# Revit family: Wood_Lockers-Salsbury_Industries-37000_Series-3_Wide_Units
name_source: partatom
category: Specialty Equipment
revit_build: Autodesk Revit 2016 (Build: 20150714_1515(x64)
units: mm (PartAtom-declared; Revit-internal decimal feet)

## family parameters
Always vertical = Yes
Cut with Voids When Loaded = No
OmniClass Number = 23.40.00.00
OmniClass Title = Equipment and Furnishings
Part Type = Normal
Room Calculation Point = No
Round Connector Dimension = Use Diameter
Shared = No
Work Plane-Based = No

## types (12) — shared parameters
Assembly Code = C1030310
Door Trim = Rubber Trim - Salsbury Finish - Textured
Hardware = Aluminum - Salsbury Finish - Black Satin
Manufacturer = Salsbury Industries
MasterFormat Code = 10 51 23
MasterFormat Title = Lockers
OmniClass 23 Number = 23.40.00.00
OmniClass 23 Title = Equipment and Furnishings
Primary Structure Materials = Particle Board Industrial Grade - Salsbury Finish - White Melamine Inlay
Secondary Structure Materials = Particle Board Industrial Grade - Salsbury Finish - Black Melamine Overlay
Type Comments = Designer Wood Lockers - Double Tier 'S' Style
URL = www.lockers.com
Unit Trim = Melamine - Salsbury Finish - Black
Version = 2.0 (07/14/17)
Width = 36.000"

## per-type parameters (varying)
| type | Base | Base Height | Depth | Description | Door Location D1 | Door Location D2 | Individual Door Height | Model | Sloping Hood Height | Unit Height |
| 37365 | Wood Locker Bases : Base - 36" W x 15" D Lockers | 4.000" | 15.000" | 3 Wide - 6 Feet High - 15 inches Deep - with Base | Wood Locker S-Style Top Doors : Double Tier Top S-Door for Six Foot High Locker | Wood Locker S-Style Bottom Doors : Double Tier Bottom S-Door for Six Foot High Locker | 42.062" | 37365 | 5.743" | 72.000" |
| 37365 - without Base | Wood Locker Bases : None | 0.000" | 15.000" | 3 Wide - 6 Feet High - 15 inches Deep - without Base | Wood Locker S-Style Top Doors : Double Tier Top S-Door for Six Foot High Locker | Wood Locker S-Style Bottom Doors : Double Tier Bottom S-Door for Six Foot High Locker | 42.062" | 37365 without Base | 5.743" | 72.000" |
| 37368 | Wood Locker Bases : Base - 36" W x 18" D Lockers | 4.000" | 18.000" | 3 Wide - 6 Feet High - 18 inches Deep - with Base | Wood Locker S-Style Top Doors : Double Tier Top S-Door for Six Foot High Locker | Wood Locker S-Style Bottom Doors : Double Tier Bottom S-Door for Six Foot High Locker | 42.062" | 37368 | 6.868" | 72.000" |
| 37368 - without Base | Wood Locker Bases : None | 0.000" | 18.000" | 3 Wide - 6 Feet High - 18 inches Deep - without Base | Wood Locker S-Style Top Doors : Double Tier Top S-Door for Six Foot High Locker | Wood Locker S-Style Bottom Doors : Double Tier Bottom S-Door for Six Foot High Locker | 42.062" | 37368 without Base | 6.868" | 72.000" |
| 37361 | Wood Locker Bases : Base - 36" W x 21" D Lockers | 4.000" | 21.000" | 3 Wide - 6 Feet High - 21 inches Deep - with Base | Wood Locker S-Style Top Doors : Double Tier Top S-Door for Six Foot High Locker | Wood Locker S-Style Bottom Doors : Double Tier Bottom S-Door for Six Foot High Locker | 42.062" | 37361 | 7.993" | 72.000" |
| 37361 - without Base | Wood Locker Bases : None | 0.000" | 21.000" | 3 Wide - 6 Feet High - 21 inches Deep - without Base | Wood Locker S-Style Top Doors : Double Tier Top S-Door for Six Foot High Locker | Wood Locker S-Style Bottom Doors : Double Tier Bottom S-Door for Six Foot High Locker | 42.062" | 37361 without Base | 7.993" | 72.000" |
| 37355 | Wood Locker Bases : Base - 36" W x 15" D Lockers | 4.000" | 15.000" | 3 Wide - 5 Feet High - 15 inches Deep - with Base | Wood Locker S-Style Top Doors : Double Tier Top S-Door for Five Foot High Locker | Wood Locker S-Style Bottom Doors : Double Tier Bottom S-Door for Five Foot High Locker | 36.062" | 37355 | 5.743" | 60.000" |
| 37355 - without Base | Wood Locker Bases : None | 0.000" | 15.000" | 3 Wide - 5 Feet High - 15 inches Deep - without Base | Wood Locker S-Style Top Doors : Double Tier Top S-Door for Five Foot High Locker | Wood Locker S-Style Bottom Doors : Double Tier Bottom S-Door for Five Foot High Locker | 36.062" | 37355 without Base | 5.743" | 60.000" |
| 37358 | Wood Locker Bases : Base - 36" W x 18" D Lockers | 4.000" | 18.000" | 3 Wide - 5 Feet High - 18 inches Deep - with Base | Wood Locker S-Style Top Doors : Double Tier Top S-Door for Five Foot High Locker | Wood Locker S-Style Bottom Doors : Double Tier Bottom S-Door for Five Foot High Locker | 36.062" | 37358 | 6.868" | 60.000" |
| 37358 - without Base | Wood Locker Bases : None | 0.000" | 18.000" | 3 Wide - 5 Feet High - 18 inches Deep - without Base | Wood Locker S-Style Top Doors : Double Tier Top S-Door for Five Foot High Locker | Wood Locker S-Style Bottom Doors : Double Tier Bottom S-Door for Five Foot High Locker | 36.062" | 37358 without Base | 6.868" | 60.000" |
| 37351 | Wood Locker Bases : Base - 36" W x 21" D Lockers | 4.000" | 21.000" | 3 Wide - 5 Feet High - 21 inches Deep - with Base | Wood Locker S-Style Top Doors : Double Tier Top S-Door for Five Foot High Locker | Wood Locker S-Style Bottom Doors : Double Tier Bottom S-Door for Five Foot High Locker | 36.062" | 37351 | 7.993" | 60.000" |
| 37351 - without Base | Wood Locker Bases : None | 0.000" | 21.000" | 3 Wide - 5 Feet High - 21 inches Deep - without Base | Wood Locker S-Style Top Doors : Double Tier Top S-Door for Five Foot High Locker | Wood Locker S-Style Bottom Doors : Double Tier Bottom S-Door for Five Foot High Locker | 36.062" | 37351 without Base | 7.993" | 60.000" |

## geometry (parser evidence)
native form markers: Sweep x40
no freeform markers — native parametric forms only
